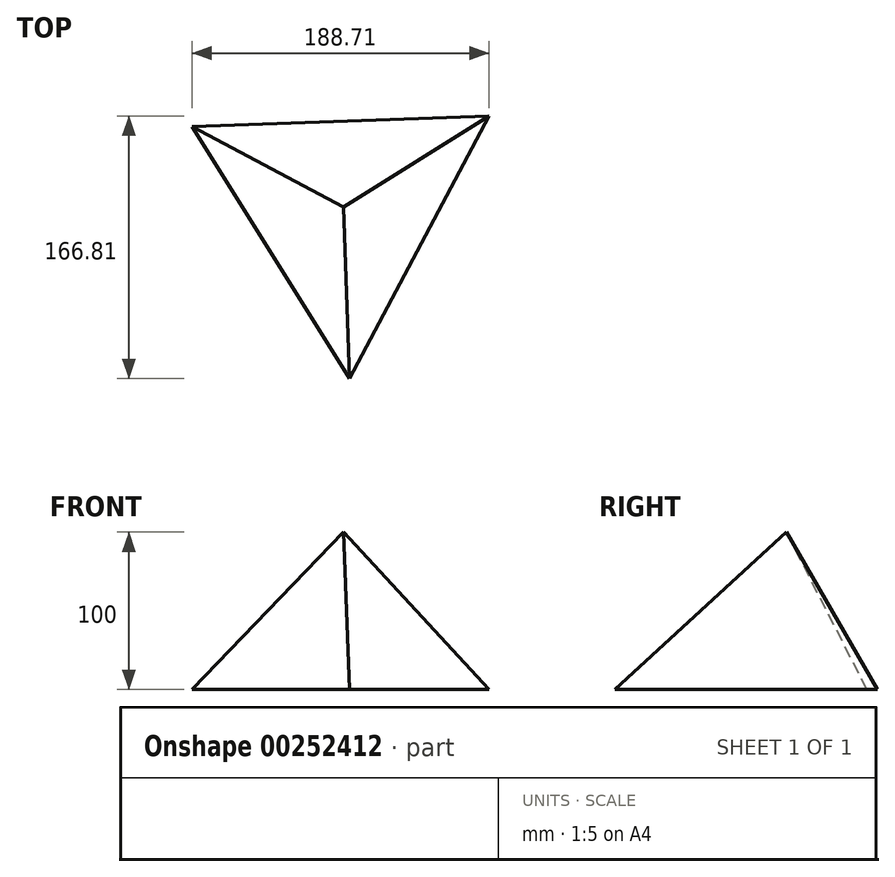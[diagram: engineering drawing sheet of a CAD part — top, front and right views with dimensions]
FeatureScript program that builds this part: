
annotation { "Feature Type Name" : "Feature", "Feature Type Description" : "" }
export const myFeature = defineFeature(function(context is Context, id is Id, definition is map)
    precondition{}
    {
        {
            var Q0;
            Q0=qCreatedBy(makeId("Top.planeOp"),FACE);
            var sketch = newSketch(context, id + "F0", { "sketchPlane" : qUnion([Q0])});
            skCircle(sketch, "E0.cCircle", {"center": v(0, 0) * mm, "radius": 109.02 * mm, "construction": true});
            skLineSegment(sketch, "E0.0", {"start": v(92.4, 57.86) * mm, "end": v(3.9, -108.95) * mm});
            skLineSegment(sketch, "E0.1", {"start": v(3.9, -108.95) * mm, "end": v(-96.3, 51.09) * mm});
            skLineSegment(sketch, "E0.2", {"start": v(-96.3, 51.09) * mm, "end": v(92.4, 57.86) * mm});
            skSolve(sketch);
        }
        {
            var Q0;
            Q0=qCreatedBy(makeId("Top.planeOp"),FACE);
            cPlane(context, id + "F1", {"entities" : qUnion([Q0]), "cplaneType" : CPlaneType.OFFSET, "offset" : 100 * mm, "width" : 152.4 * mm, "height" : 152.4 * mm});
        }
        {
            var Q0;
            Q0=qCreatedBy(id+"F1.planeOp",FACE);
            var sketch = newSketch(context, id + "F2", { "sketchPlane" : qUnion([Q0])});
            skPoint(sketch, "E1", {"position": v(0, 0) * mm});
            skSolve(sketch);
        }
        {
            var Q0;
            Q0=makeQuery(id+"F0.imprint","IMPRINT",FACE,{"disambiguationData":[TD([[makeQuery(id+"F0.imprint","IMPRINT",EDGE,{"derivedFrom":sQuery(id+"F0.wireOp",EDGE,"E0.0")}),-1.0]])]});
            var Q1;
            Q1=sQuery(id+"F2.wireOp",VERTEX,"E1");
            loft(context, id + "F3", {"sheetProfilesArray" : [{ "sheetProfileEntities" : qUnion([Q0]) }, { "sheetProfileEntities" : qUnion([Q1]) }]});
        }
    });
